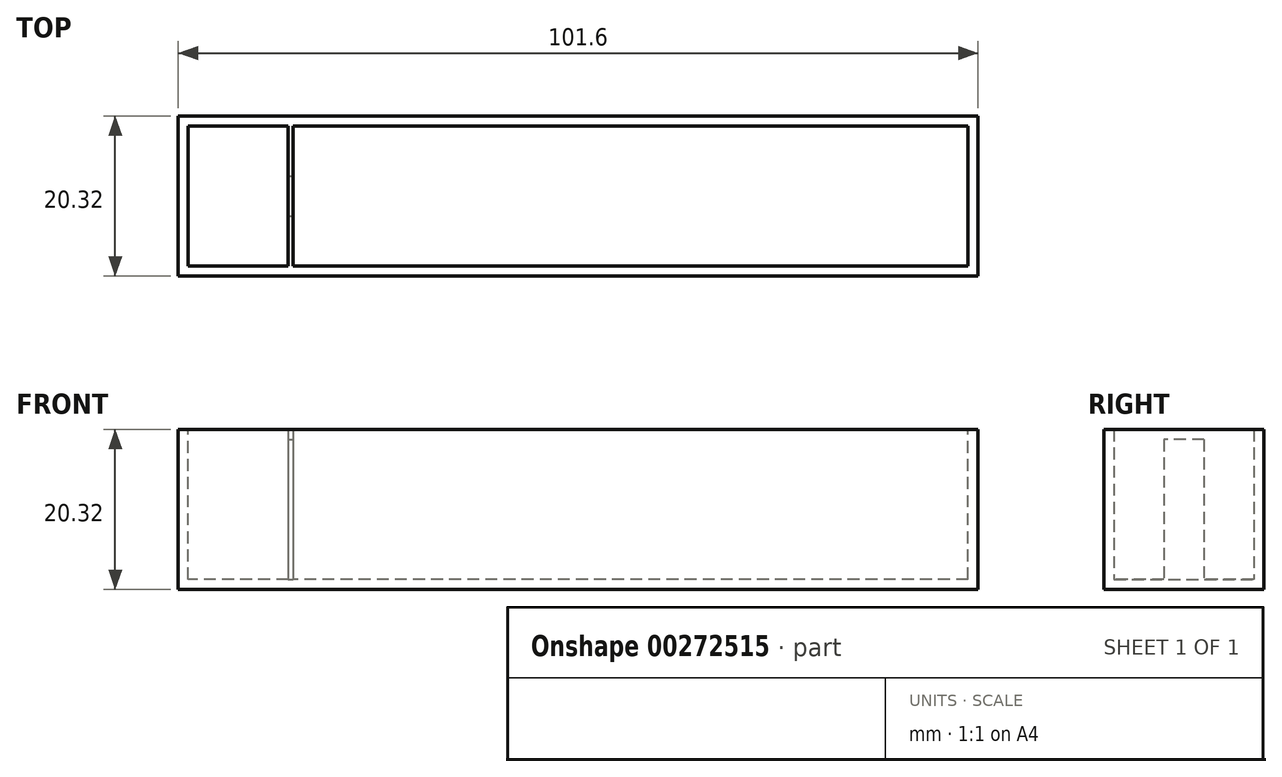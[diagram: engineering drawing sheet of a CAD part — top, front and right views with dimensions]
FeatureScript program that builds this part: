
annotation { "Feature Type Name" : "Feature", "Feature Type Description" : "" }
export const myFeature = defineFeature(function(context is Context, id is Id, definition is map)
    precondition{}
    {
        {
            var Q0;
            Q0=qCreatedBy(makeId("Front.planeOp"),FACE);
            var sketch = newSketch(context, id + "F0", { "sketchPlane" : qUnion([Q0])});
            skLineSegment(sketch, "E0.bottom", {"start": v(50.8, 10.16) * mm, "end": v(-50.8, 10.16) * mm});
            skLineSegment(sketch, "E0.top", {"start": v(50.8, -10.16) * mm, "end": v(-50.8, -10.16) * mm});
            skLineSegment(sketch, "E0.left", {"start": v(50.8, 10.16) * mm, "end": v(50.8, -10.16) * mm});
            skLineSegment(sketch, "E0.right", {"start": v(-50.8, 10.16) * mm, "end": v(-50.8, -10.16) * mm});
            skPoint(sketch, "E0.middle", {"position": v(0, 0) * mm});
            skSolve(sketch);
        }
        {
            var Q0;
            Q0 = qSketchRegion(id + "F0", true);
            extrude(context, id + "F1", {"entities" : qUnion([Q0]), "depth" : 10.16 * mm, "hasSecondDirection" : true, "secondDirectionOppositeDirection" : true, "secondDirectionDepth" : 10.16 * mm});
        }
        {
            var Q0;
            Q0=makeQuery(id+"F1.opExtrude","SWEPT_FACE",FACE,{"disambiguationData":[OSD([sQuery(id+"F0.wireOp",EDGE,"E0.bottom")])]});
            var sketch = newSketch(context, id + "F2", { "sketchPlane" : qUnion([Q0])});
            skLineSegment(sketch, "E1.bottom", {"start": v(49.53, -8.89) * mm, "end": v(-49.53, -8.9) * mm});
            skLineSegment(sketch, "E1.top", {"start": v(49.53, 8.9) * mm, "end": v(-49.53, 8.89) * mm});
            skLineSegment(sketch, "E1.left", {"start": v(49.53, -8.89) * mm, "end": v(49.53, 8.9) * mm});
            skLineSegment(sketch, "E1.right", {"start": v(-49.53, -8.9) * mm, "end": v(-49.53, 8.89) * mm});
            skPoint(sketch, "E1.middle", {"position": v(0, 0) * mm});
            skSolve(sketch);
        }
        {
            var Q0;
            Q0 = qSketchRegion(id + "F2", true);
            extrude(context, id + "F3", {"entities" : qUnion([Q0]), "operationType" : NewBodyOperationType.REMOVE, "oppositeDirection" : true, "depth" : 19.05 * mm});
        }
        {
            var Q0;
            Q0=makeQuery(id+"F3.boolean.opBoolean","COPY",FACE,{"derivedFrom":makeQuery(id+"F3.opExtrude","CAP_FACE",FACE,{"disambiguationData":[OSD([sQuery(id+"F2.wireOp",EDGE,"E1.bottom"),sQuery(id+"F2.wireOp",EDGE,"E1.top"),sQuery(id+"F2.wireOp",EDGE,"E1.left"),sQuery(id+"F2.wireOp",EDGE,"E1.right")])],"isStart":false})});
            var sketch = newSketch(context, id + "F4", { "sketchPlane" : qUnion([Q0])});
            skLineSegment(sketch, "E2.bottom", {"start": v(-49.53, 8.89) * mm, "end": v(-36.83, 8.89) * mm});
            skLineSegment(sketch, "E2.top", {"start": v(-49.53, -8.9) * mm, "end": v(-36.83, -8.9) * mm});
            skLineSegment(sketch, "E2.left", {"start": v(-49.53, 8.89) * mm, "end": v(-49.53, -8.9) * mm});
            skLineSegment(sketch, "E2.right", {"start": v(-36.83, 8.89) * mm, "end": v(-36.83, 2.54) * mm});
            skLineSegment(sketch, "E3.bottom", {"start": v(-36.83, 8.89) * mm, "end": v(-36.2, 8.89) * mm});
            skLineSegment(sketch, "E3.top", {"start": v(-36.83, -8.9) * mm, "end": v(-36.2, -8.9) * mm});
            skLineSegment(sketch, "E3.right", {"start": v(-36.2, 8.89) * mm, "end": v(-36.2, 2.54) * mm});
            skLineSegment(sketch, "E4.bottom", {"start": v(-36.83, 2.54) * mm, "end": v(-36.2, 2.54) * mm});
            skLineSegment(sketch, "E4.top", {"start": v(-36.83, -2.54) * mm, "end": v(-36.2, -2.54) * mm});
            skLineSegment(sketch, "E5.trimOffspring", {"start": v(-36.83, -2.54) * mm, "end": v(-36.83, -8.9) * mm});
            skLineSegment(sketch, "E6.trimOffspring", {"start": v(-36.2, -2.54) * mm, "end": v(-36.2, -8.9) * mm});
            skLineSegment(sketch, "E7.left", {"start": v(-36.83, 2.54) * mm, "end": v(-36.83, -2.54) * mm});
            skLineSegment(sketch, "E7.right", {"start": v(-36.2, 2.54) * mm, "end": v(-36.2, -2.54) * mm});
            skSolve(sketch);
        }
        {
            var Q0;
            Q0=makeQuery(id+"F4.imprint","IMPRINT",FACE,{"disambiguationData":[TD([[makeQuery(id+"F4.imprint","IMPRINT",EDGE,{"derivedFrom":sQuery(id+"F4.wireOp",EDGE,"E3.top")}),-1.0]])]});
            var Q1;
            Q1=makeQuery(id+"F4.imprint","IMPRINT",FACE,{"disambiguationData":[TD([[makeQuery(id+"F4.imprint","IMPRINT",EDGE,{"derivedFrom":sQuery(id+"F4.wireOp",EDGE,"E3.bottom")}),1.0]])]});
            extrude(context, id + "F5", {"entities" : qUnion([Q0, Q1]), "operationType" : NewBodyOperationType.ADD, "depth" : 19.05 * mm});
        }
        {
            var Q0;
            Q0=makeQuery(id+"F4.imprint","IMPRINT",FACE,{"disambiguationData":[TD([[makeQuery(id+"F4.imprint","IMPRINT",EDGE,{"derivedFrom":sQuery(id+"F4.wireOp",EDGE,"E4.bottom")}),-1.0]])]});
            extrude(context, id + "F6", {"entities" : qUnion([Q0]), "operationType" : NewBodyOperationType.ADD, "depth" : 19.05 * mm, "hasSecondDirection" : true, "secondDirectionOppositeDirection" : false, "secondDirectionDepth" : 17.78 * mm});
        }
    });
